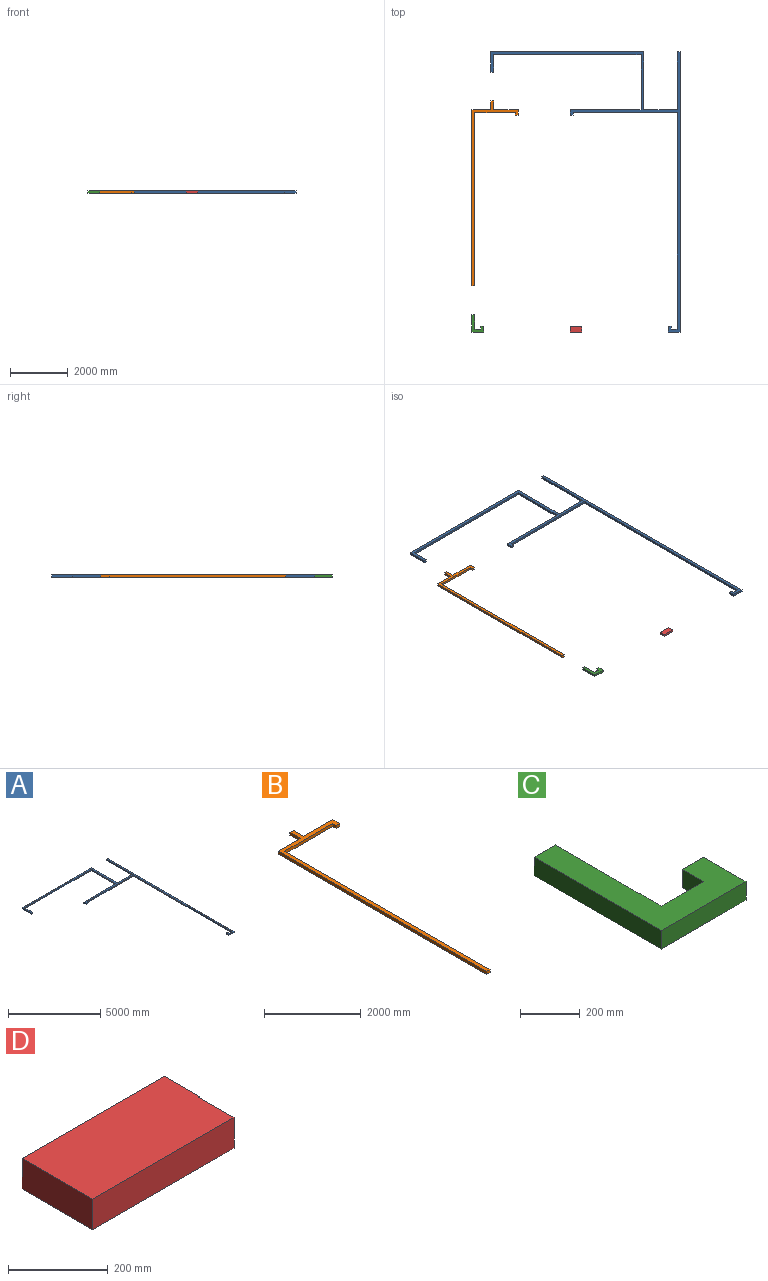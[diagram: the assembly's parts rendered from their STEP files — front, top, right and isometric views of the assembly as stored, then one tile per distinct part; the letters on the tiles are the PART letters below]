
ASSEMBLY  parts=4 mates=10
PART A: 24 faces, bbox 6550x9700x75 mm
  f0: plane 2000x75mm, normal (-1,0,0), area 150000mm2, adj f1,f21,f22,f23
  f1: plane 1150x75mm, normal (0,1,0), area 86250mm2, adj f0,f2,f22,f23
  f2: plane 2000x75mm, normal (1,0,0), area 150000mm2, adj f1,f3,f22,f23
  f3: plane 5300x75mm, normal (0,1,0), area 397500mm2, adj f2,f4,f22,f23
  f4: plane 700x75mm, normal (-1,0,0), area 52500mm2, adj f3,f5,f22,f23
  f5: plane 100x75mm, normal (0,-1,0), area 7500mm2, adj f4,f6,f22,f23
  f6: plane 600x75mm, normal (1,0,0), area 45000mm2, adj f5,f7,f22,f23
  f7: plane 5100x75mm, normal (0,-1,0), area 382500mm2, adj f6,f8,f22,f23
  f8: plane 1900x75mm, normal (-1,0,0), area 142500mm2, adj f7,f9,f22,f23
  f9: plane 2450x75mm, normal (0,1,0), area 183750mm2, adj f8,f10,f22,f23
  f10: plane 200x75mm, normal (-1,0,0), area 15000mm2, adj f9,f11,f22,f23
  f11: plane 100x75mm, normal (0,-1,0), area 7500mm2, adj f10,f12,f22,f23
  f12: plane 100x75mm, normal (1,0,0), area 7500mm2, adj f11,f13,f22,f23
  f13: plane 3600x75mm, normal (0,-1,0), area 270000mm2, adj f12,f14,f22,f23
  f14: plane 7500x75mm, normal (-1,0,0), area 562500mm2, adj f13,f15,f22,f23
  f15: plane 200x75mm, normal (0,1,0), area 15000mm2, adj f14,f16,f22,f23
  f16: plane 100x75mm, normal (1,0,0), area 7500mm2, adj f15,f17,f22,f23
  f17: plane 100x75mm, normal (0,1,0), area 7500mm2, adj f16,f18,f22,f23
  f18: plane 200x75mm, normal (-1,0,0), area 15000mm2, adj f17,f19,f22,f23
  f19: plane 400x75mm, normal (0,-1,0), area 30000mm2, adj f18,f20,f22,f23
  f20: plane 9700x75mm, normal (1,0,0), area 727500mm2, adj f19,f21,f22,f23
  f21: plane 100x75mm, normal (0,1,0), area 7500mm2, adj f0,f20,f22,f23
  f22: plane 9700x6550mm, normal (0,0,1), area 2170000mm2, adj f0,f1,f2,f3,f4,f5,f6,f7
  f23: plane 9700x6550mm, normal (0,0,-1), area 2170000mm2, adj f0,f1,f2,f3,f4,f5,f6,f7
PART B: 14 faces, bbox 1600x6400x75 mm
  f0: plane 300x75mm, normal (-1,0,0), area 22500mm2, adj f1,f11,f12,f13
  f1: plane 650x75mm, normal (0,1,0), area 48750mm2, adj f0,f2,f12,f13
  f2: plane 6100x75mm, normal (-1,0,0), area 457500mm2, adj f1,f3,f12,f13
  f3: plane 100x75mm, normal (0,-1,0), area 7500mm2, adj f2,f4,f12,f13
  f4: plane 6000x75mm, normal (1,0,0), area 450000mm2, adj f3,f5,f12,f13
  f5: plane 1400x75mm, normal (0,-1,0), area 105000mm2, adj f4,f6,f12,f13
  f6: plane 100x75mm, normal (-1,0,0), area 7500mm2, adj f5,f7,f12,f13
  f7: plane 100x75mm, normal (0,-1,0), area 7500mm2, adj f6,f8,f12,f13
  f8: plane 200x75mm, normal (1,0,0), area 15000mm2, adj f7,f9,f12,f13
  f9: plane 850x75mm, normal (0,1,0), area 63750mm2, adj f8,f10,f12,f13
  f10: plane 300x75mm, normal (1,0,0), area 22500mm2, adj f9,f11,f12,f13
  f11: plane 100x75mm, normal (0,1,0), area 7500mm2, adj f0,f10,f12,f13
  f12: plane 6400x1600mm, normal (0,0,1), area 800000mm2, adj f0,f1,f2,f3,f4,f5,f6,f7
  f13: plane 6400x1600mm, normal (0,0,-1), area 800000mm2, adj f0,f1,f2,f3,f4,f5,f6,f7
PART C: 10 faces, bbox 400x600x75 mm
  f0: plane 200x75mm, normal (1,0,0), area 15000mm2, adj f1,f7,f8,f9
  f1: plane 100x75mm, normal (0,1,0), area 7500mm2, adj f0,f2,f8,f9
  f2: plane 100x75mm, normal (-1,0,0), area 7500mm2, adj f1,f3,f8,f9
  f3: plane 200x75mm, normal (0,1,0), area 15000mm2, adj f2,f4,f8,f9
  f4: plane 500x75mm, normal (1,0,0), area 37500mm2, adj f3,f5,f8,f9
  f5: plane 100x75mm, normal (0,1,0), area 7500mm2, adj f4,f6,f8,f9
  f6: plane 600x75mm, normal (-1,0,0), area 45000mm2, adj f5,f7,f8,f9
  f7: plane 400x75mm, normal (0,-1,0), area 30000mm2, adj f0,f6,f8,f9
  f8: plane 600x400mm, normal (0,0,1), area 100000mm2, adj f0,f1,f2,f3,f4,f5,f6,f7
  f9: plane 600x400mm, normal (0,0,-1), area 100000mm2, adj f0,f1,f2,f3,f4,f5,f6,f7
PART D: 8 faces, bbox 402.7x200x75 mm
  f0: plane 200x75mm, normal (-1,0,0), area 15000mm2, adj f1,f5,f6,f7
  f1: plane 400x75mm, normal (0,-1,0), area 30000mm2, adj f0,f2,f6,f7
  f2: plane 100x75mm, normal (1,0,0), area 7500mm2, adj f1,f3,f6,f7
  f3: plane 75x2.7mm, normal (0,-1,0), area 202.7mm2, adj f2,f4,f6,f7
  f4: plane 100x75mm, normal (1,0,0), area 7500mm2, adj f3,f5,f6,f7
  f5: plane 402.7x75mm, normal (0,1,0), area 30202.7mm2, adj f0,f4,f6,f7
  f6: plane 402.7x200mm, normal (0,0,1), area 80270.2mm2, adj f0,f1,f2,f3,f4,f5
  f7: plane 402.7x200mm, normal (0,0,-1), area 80270.2mm2, adj f0,f1,f2,f3,f4,f5
PLACE A t=(-1767.56,-1254.16,989.27)mm
PLACE B t=(-1767.56,-1254.16,989.27)mm
PLACE C t=(-1767.56,-1254.16,989.27)mm
PLACE D t=(-1767.56,-1254.16,989.27)mm
MATE planar C.f4 <-> B.f4  axis (1,0,0) through (-5267.79,-4532.79,1026.77)mm
MATE planar B.f7 <-> A.f11  axis (0,-1,0) through (-3817.79,2617.21,1026.77)mm
MATE planar D.f6 <-> C.f8  axis (0,0,1) through (-1767.11,-4782.62,1064.27)mm
MATE parallel C.f0 <-> D.f0  axis (1,0,0) through (-4967.79,-4782.79,1026.77)mm
MATE planar B.f12 <-> A.f22  axis (0,0,1) through (-3817.79,2617.21,1064.27)mm
MATE planar B.f0 <-> A.f4  axis (-1,0,0) through (-4717.79,2967.21,1026.77)mm
MATE planar C.f7 <-> A.f19  axis (0,-1,0) through (-5167.79,-4882.79,1026.77)mm
MATE planar D.f1 <-> C.f7  axis (0,-1,0) through (-1567.79,-4882.79,1064.27)mm
MATE parallel D.f3 <-> C.f7  axis (0,1,0) through (-1967.79,-4782.79,1064.27)mm
MATE planar C.f8 <-> B.f12  axis (0,0,1) through (-4967.79,-4882.79,1064.27)mm
